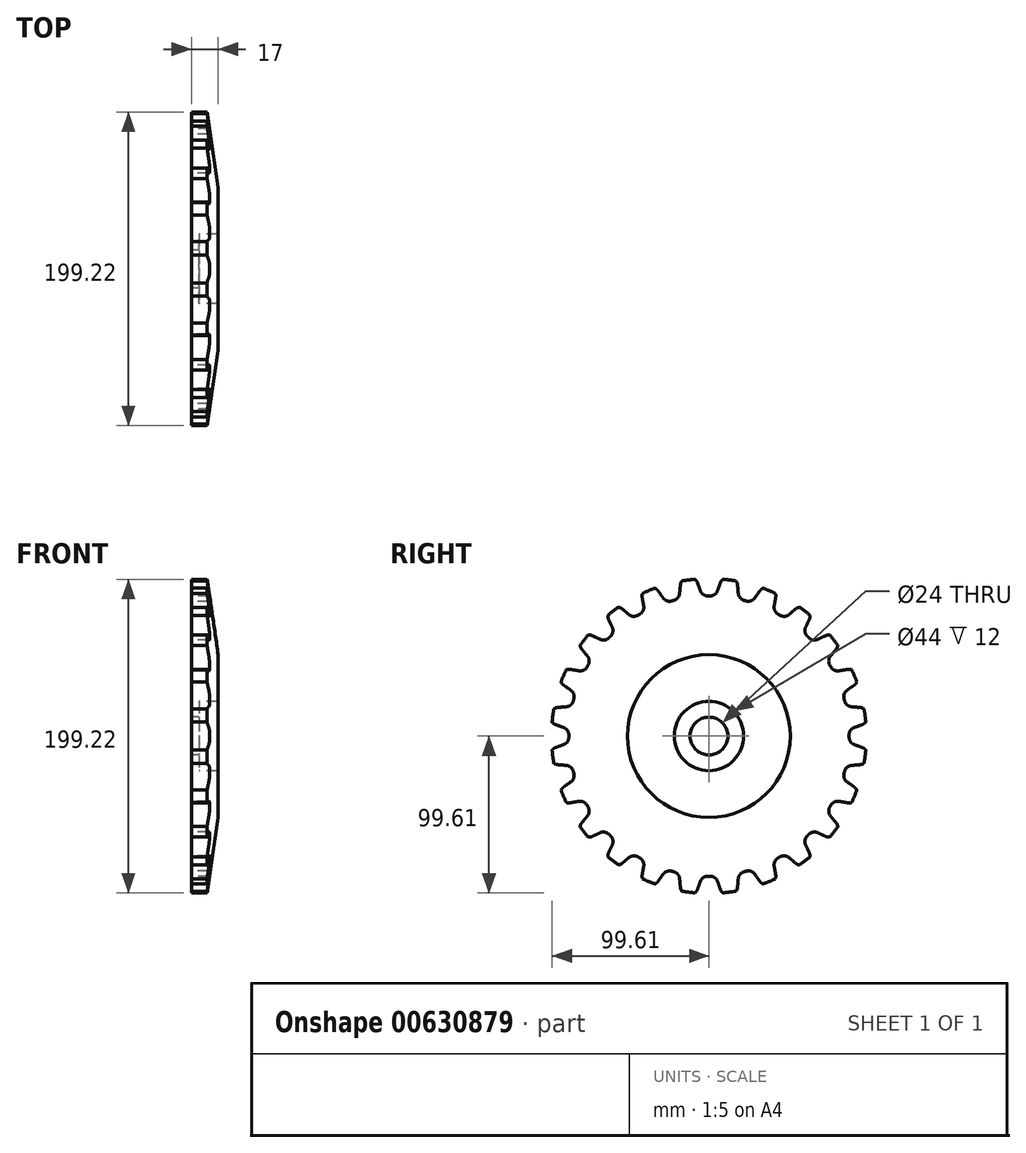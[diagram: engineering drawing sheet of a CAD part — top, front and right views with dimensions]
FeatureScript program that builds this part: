
annotation { "Feature Type Name" : "Feature", "Feature Type Description" : "" }
export const myFeature = defineFeature(function(context is Context, id is Id, definition is map)
    precondition{}
    {
        {
            var Q0;
            Q0=qCreatedBy(makeId("Front.planeOp"),FACE);
            var sketch = newSketch(context, id + "F0", { "sketchPlane" : qUnion([Q0])});
            skLineSegment(sketch, "E0", {"start": v(0, 0) * mm, "end": v(0, 100) * mm});
            skLineSegment(sketch, "E1", {"start": v(0, 100) * mm, "end": v(0, 100) * mm});
            skLineSegment(sketch, "E2", {"start": v(0, 100) * mm, "end": v(10, 100) * mm});
            skLineSegment(sketch, "E3", {"start": v(10, 100) * mm, "end": v(17, 51.68) * mm});
            skLineSegment(sketch, "E4", {"start": v(17, 51.68) * mm, "end": v(17, 22) * mm});
            skLineSegment(sketch, "E5", {"start": v(17, 22) * mm, "end": v(5, 22) * mm});
            skLineSegment(sketch, "E6", {"start": v(5, 22) * mm, "end": v(5, 12) * mm});
            skLineSegment(sketch, "E7", {"start": v(5, 12) * mm, "end": v(0, 12) * mm});
            skPoint(sketch, "E8", {"position": v(0, 12) * mm});
            skPoint(sketch, "E9", {"position": v(0, 0) * mm});
            skLineSegment(sketch, "E10", {"start": v(0, 0) * mm, "end": v(13.17, 0) * mm});
            skSolve(sketch);
        }
        {
            var Q0;
            {var subQ0=sQuery(id+"F0.wireOp",EDGE,"E2");Q0=makeQuery(id+"F0.imprint","IMPRINT",FACE,{"disambiguationData":[TD([[makeQuery(id+"F0.imprint","IMPRINT",EDGE,{"derivedFrom":subQ0}),-1.0]])]});}
            var Q1;
            Q1=sQuery(id+"F0.wireOp",EDGE,"E10");
            revolve(context, id + "F1", {"entities" : qUnion([Q0]), "axis" : qUnion([Q1]), "revolveType" : RevolveType.FULL});
        }
        {
            var Q0;
            Q0=qCreatedBy(makeId("Right.planeOp"),FACE);
            var sketch = newSketch(context, id + "F2", { "sketchPlane" : qUnion([Q0])});
            skLineSegment(sketch, "E11", {"start": v(0, 0) * mm, "end": v(0, 122.66) * mm});
            skLineSegment(sketch, "E12", {"start": v(0, 104.01) * mm, "end": v(9.7, 104.01) * mm});
            skLineSegment(sketch, "E13", {"start": v(7.3, 97.43) * mm, "end": v(5.44, 92.3) * mm});
            skLineSegment(sketch, "E14", {"start": v(0.74, 89.01) * mm, "end": v(0, 89.01) * mm});
            skPoint(sketch, "E15.visualSharp", {"position": v(4.24, 89.01) * mm});
            skArc(sketch, "E15.filletArc", {"start": v(0.74, 89.01) * mm, "mid": v(3.6, 89.92) * mm, "end": v(5.44, 92.3) * mm});
            skLineSegment(sketch, "E16.MirrorCS", {"start": v(0, 104.01) * mm, "end": v(-9.7, 104.01) * mm});
            skArc(sketch, "E17.MirrorCS", {"start": v(-0.74, 89.01) * mm, "mid": v(-3.6, 89.92) * mm, "end": v(-5.44, 92.3) * mm});
            skLineSegment(sketch, "E18.MirrorCS", {"start": v(-0.74, 89.01) * mm, "end": v(0, 89.01) * mm});
            skPoint(sketch, "E19", {"position": v(7.94, 99.18) * mm});
            skLineSegment(sketch, "E20", {"start": v(9.57, 100.09) * mm, "end": v(10.66, 100.7) * mm});
            skLineSegment(sketch, "E21", {"start": v(9.7, 104.01) * mm, "end": v(10.66, 100.7) * mm});
            skPoint(sketch, "E22.MirrorCS.end.orphan", {"position": v(-5.44, 92.3) * mm});
            skPoint(sketch, "E22.MirrorCS.start.orphan", {"position": v(-9.7, 104.01) * mm});
            skArc(sketch, "E23.filletArc", {"start": v(9.57, 100.09) * mm, "mid": v(8.2, 98.96) * mm, "end": v(7.3, 97.43) * mm});
            skPoint(sketch, "E24.MirrorP", {"position": v(-7.94, 99.18) * mm});
            skLineSegment(sketch, "E25.MirrorCS", {"start": v(-9.7, 104.01) * mm, "end": v(-10.66, 100.7) * mm});
            skLineSegment(sketch, "E26.MirrorCS", {"start": v(-9.57, 100.09) * mm, "end": v(-10.66, 100.7) * mm});
            skArc(sketch, "E27.MirrorCS", {"start": v(-9.57, 100.09) * mm, "mid": v(-8.2, 98.96) * mm, "end": v(-7.3, 97.43) * mm});
            skLineSegment(sketch, "E28.MirrorCS", {"start": v(-7.3, 97.43) * mm, "end": v(-5.44, 92.3) * mm});
            skPoint(sketch, "E29", {"position": v(-8.82, 99.58) * mm});
            skSolve(sketch);
        }
        {
            var Q0;
            Q0 = qSketchRegion(id + "F2", true);
            extrude(context, id + "F3", {"entities" : qUnion([Q0]), "operationType" : NewBodyOperationType.REMOVE, "oppositeDirection" : true, "depth" : 25 * mm, "offsetDistance" : 25 * mm});
        }
        {
            var Q0;
            Q0 = qSketchRegion(id + "F2", true);
            extrude(context, id + "F4", {"entities" : qUnion([Q0]), "operationType" : NewBodyOperationType.REMOVE, "depth" : 25 * mm, "offsetDistance" : 25 * mm});
        }
        {
            var Q0;
            Q0=makeQuery(id+"F4.boolean.opBoolean","COPY",FACE,{"derivedFrom":makeQuery(id+"F4.opExtrude","SWEPT_FACE",FACE,{"disambiguationData":[OSD([sQuery(id+"F2.wireOp",EDGE,"E27.MirrorCS")])]})});
            var Q1;
            Q1=makeQuery(id+"F4.boolean.opBoolean","COPY",FACE,{"derivedFrom":makeQuery(id+"F4.opExtrude","SWEPT_FACE",FACE,{"disambiguationData":[OSD([sQuery(id+"F2.wireOp",EDGE,"E28.MirrorCS")])]})});
            var Q2;
            Q2=makeQuery(id+"F4.boolean.opBoolean","COPY",FACE,{"derivedFrom":makeQuery(id+"F4.opExtrude","SWEPT_FACE",FACE,{"disambiguationData":[OSD([sQuery(id+"F2.wireOp",EDGE,"E17.MirrorCS")])]})});
            var Q3;
            Q3=makeQuery(id+"F4.boolean.opBoolean","COPY",FACE,{"derivedFrom":makeQuery(id+"F4.opExtrude","SWEPT_FACE",FACE,{"disambiguationData":[OSD([sQuery(id+"F2.wireOp",EDGE,"E14"),sQuery(id+"F2.wireOp",EDGE,"E18.MirrorCS")])]})});
            var Q4;
            Q4=makeQuery(id+"F4.boolean.opBoolean","COPY",FACE,{"derivedFrom":makeQuery(id+"F4.opExtrude","SWEPT_FACE",FACE,{"disambiguationData":[OSD([sQuery(id+"F2.wireOp",EDGE,"E15.filletArc")])]})});
            var Q5;
            Q5=makeQuery(id+"F4.boolean.opBoolean","COPY",FACE,{"derivedFrom":makeQuery(id+"F4.opExtrude","SWEPT_FACE",FACE,{"disambiguationData":[OSD([sQuery(id+"F2.wireOp",EDGE,"E13")])]})});
            var Q6;
            Q6=makeQuery(id+"F4.boolean.opBoolean","COPY",FACE,{"derivedFrom":makeQuery(id+"F4.opExtrude","SWEPT_FACE",FACE,{"disambiguationData":[OSD([sQuery(id+"F2.wireOp",EDGE,"E23.filletArc")])]})});
            var Q7;
            Q7=makeQuery(id+"F1.opRevolve","SWEPT_FACE",FACE,{"disambiguationData":[OSD([sQuery(id+"F0.wireOp",EDGE,"E2")])]});
            circularPattern(context, id + "F5", {"patternType" : PatternType.FACE, "faces" : qUnion([Q0, Q1, Q2, Q3, Q4, Q5, Q6]), "axis" : qUnion([Q7]), "angle" : 360 * degree, "instanceCount" : 48, "equalSpace" : true});
        }
    });
